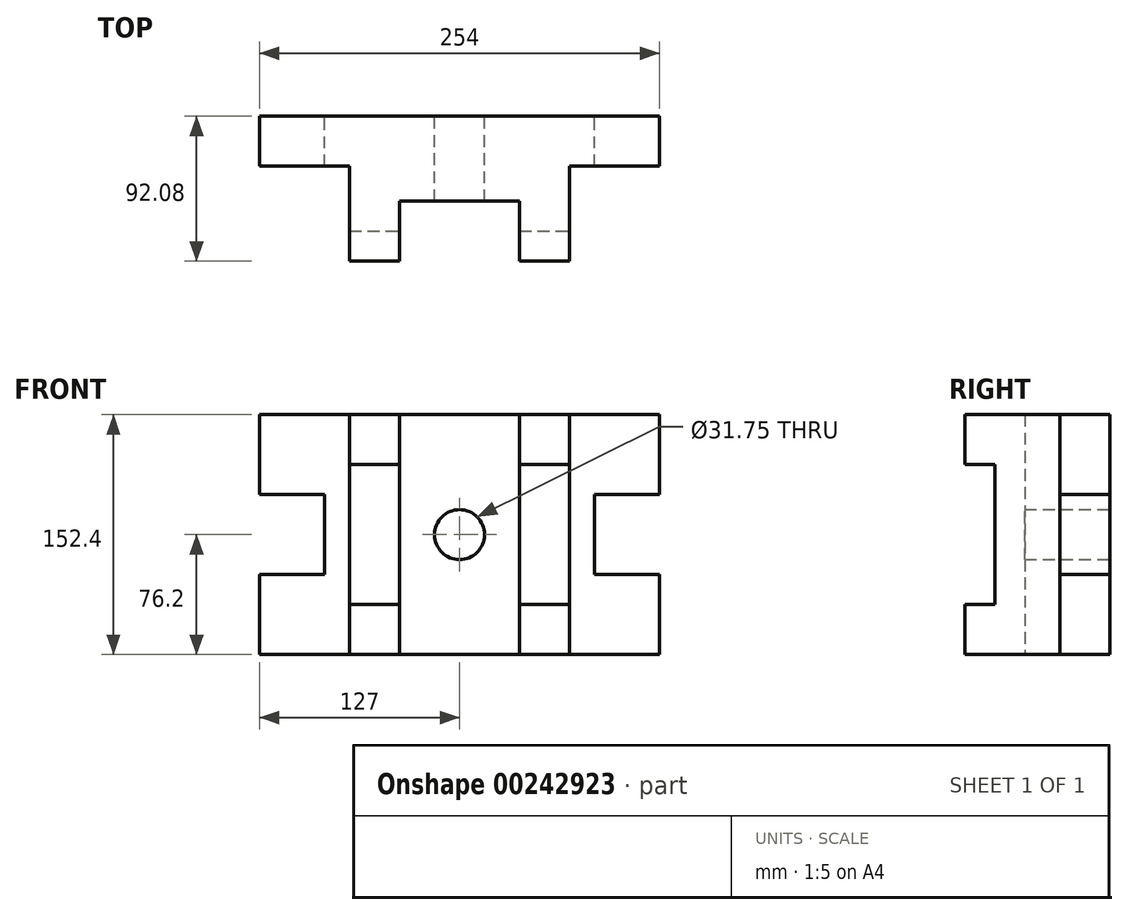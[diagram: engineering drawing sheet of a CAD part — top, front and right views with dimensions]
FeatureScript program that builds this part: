
annotation { "Feature Type Name" : "Feature", "Feature Type Description" : "" }
export const myFeature = defineFeature(function(context is Context, id is Id, definition is map)
    precondition{}
    {
        {
            var Q0;
            Q0=qCreatedBy(makeId("Front.planeOp"),FACE);
            var sketch = newSketch(context, id + "F0", { "sketchPlane" : qUnion([Q0])});
            skLineSegment(sketch, "E0.bottom", {"start": v(127, -76.2) * mm, "end": v(-127, -76.2) * mm});
            skLineSegment(sketch, "E0.top", {"start": v(127, 76.2) * mm, "end": v(-127, 76.2) * mm});
            skLineSegment(sketch, "E0.left", {"start": v(127, -76.2) * mm, "end": v(127, -25.4) * mm});
            skLineSegment(sketch, "E0.right", {"start": v(-127, -76.2) * mm, "end": v(-127, -25.18) * mm});
            skPoint(sketch, "E0.middle", {"position": v(0, 0) * mm});
            skLineSegment(sketch, "E1", {"start": v(-127, -25.18) * mm, "end": v(-127, -25.4) * mm});
            skLineSegment(sketch, "E2", {"start": v(-69.85, 76.2) * mm, "end": v(-69.85, -76.2) * mm});
            skLineSegment(sketch, "E3", {"start": v(-38.1, 76.2) * mm, "end": v(-38.1, -76.2) * mm});
            skLineSegment(sketch, "E4", {"start": v(38.1, 76.2) * mm, "end": v(38.1, -76.2) * mm});
            skLineSegment(sketch, "E5", {"start": v(69.85, -76.2) * mm, "end": v(69.85, 76.2) * mm});
            skLineSegment(sketch, "E6.bottom", {"start": v(-127, 25.4) * mm, "end": v(-85.73, 25.4) * mm});
            skLineSegment(sketch, "E6.top", {"start": v(-127, -25.18) * mm, "end": v(-85.73, -25.18) * mm});
            skLineSegment(sketch, "E6.right", {"start": v(-85.73, 25.4) * mm, "end": v(-85.73, -25.18) * mm});
            skLineSegment(sketch, "E7.bottom", {"start": v(127, 25.4) * mm, "end": v(85.72, 25.4) * mm});
            skLineSegment(sketch, "E7.top", {"start": v(127, -25.4) * mm, "end": v(85.72, -25.4) * mm});
            skLineSegment(sketch, "E7.right", {"start": v(85.72, 25.4) * mm, "end": v(85.72, -25.4) * mm});
            skLineSegment(sketch, "E8", {"start": v(127, -25.4) * mm, "end": v(127, -76.2) * mm});
            skLineSegment(sketch, "E9", {"start": v(-69.85, 44.45) * mm, "end": v(-38.1, 44.45) * mm});
            skLineSegment(sketch, "E10", {"start": v(-69.85, -44.45) * mm, "end": v(-38.1, -44.45) * mm});
            skLineSegment(sketch, "E11", {"start": v(38.1, -44.45) * mm, "end": v(69.85, -44.45) * mm});
            skCircle(sketch, "E12", {"center": v(0, 0) * mm, "radius": 15.88 * mm});
            skLineSegment(sketch, "E13", {"start": v(38.1, 44.45) * mm, "end": v(69.85, 44.45) * mm});
            skLineSegment(sketch, "E14.trimOffspring", {"start": v(127, 25.4) * mm, "end": v(127, 76.2) * mm});
            skLineSegment(sketch, "E15.trimOffspring", {"start": v(-127, 25.4) * mm, "end": v(-127, 76.2) * mm});
            skSolve(sketch);
        }
        {
            var Q0;
            {var subQ7=sQuery(id+"F0.wireOp",EDGE,"E0.right");Q0=makeQuery(id+"F0.imprint","IMPRINT",FACE,{"disambiguationData":[TD([[makeQuery(id+"F0.imprint","IMPRINT",EDGE,{"derivedFrom":subQ7}),-1.0]])]});}
            var Q1;
            Q1=makeQuery(id+"F0.imprint","IMPRINT",FACE,{"disambiguationData":[TD([[makeQuery(id+"F0.imprint","IMPRINT",EDGE,{"derivedFrom":sQuery(id+"F0.wireOp",EDGE,"E7.bottom")}),-1.0]])]});
            extrude(context, id + "F1", {"entities" : qUnion([Q0, Q1]), "depth" : 31.75 * mm});
        }
        {
            var Q0;
            {var subQ5=sQuery(id+"F0.wireOp",EDGE,"E9");Q0=makeQuery(id+"F0.imprint","IMPRINT",FACE,{"disambiguationData":[TD([[makeQuery(id+"F0.imprint","IMPRINT",EDGE,{"derivedFrom":subQ5}),1.0]])]});}
            var Q1;
            {var subQ5=sQuery(id+"F0.wireOp",EDGE,"E10");Q1=makeQuery(id+"F0.imprint","IMPRINT",FACE,{"disambiguationData":[TD([[makeQuery(id+"F0.imprint","IMPRINT",EDGE,{"derivedFrom":subQ5}),-1.0]])]});}
            var Q2;
            {var subQ5=sQuery(id+"F0.wireOp",EDGE,"E11");Q2=makeQuery(id+"F0.imprint","IMPRINT",FACE,{"disambiguationData":[TD([[makeQuery(id+"F0.imprint","IMPRINT",EDGE,{"derivedFrom":subQ5}),-1.0]])]});}
            var Q3;
            {var subQ5=sQuery(id+"F0.wireOp",EDGE,"E13");Q3=makeQuery(id+"F0.imprint","IMPRINT",FACE,{"disambiguationData":[TD([[makeQuery(id+"F0.imprint","IMPRINT",EDGE,{"derivedFrom":subQ5}),1.0]])]});}
            extrude(context, id + "F2", {"entities" : qUnion([Q0, Q1, Q2, Q3]), "depth" : 92.07 * mm});
        }
        {
            var Q0;
            {var subQ0=sQuery(id+"F0.wireOp",EDGE,"E9");Q0=makeQuery(id+"F0.imprint","IMPRINT",FACE,{"disambiguationData":[TD([[makeQuery(id+"F0.imprint","IMPRINT",EDGE,{"derivedFrom":subQ0}),-1.0]])]});}
            var Q1;
            {var subQ0=sQuery(id+"F0.wireOp",EDGE,"E11");Q1=makeQuery(id+"F0.imprint","IMPRINT",FACE,{"disambiguationData":[TD([[makeQuery(id+"F0.imprint","IMPRINT",EDGE,{"derivedFrom":subQ0}),1.0]])]});}
            extrude(context, id + "F3", {"entities" : qUnion([Q0, Q1]), "operationType" : NewBodyOperationType.ADD, "depth" : 73.02 * mm});
        }
        {
            var Q0;
            {var subQ0=sQuery(id+"F0.wireOp",EDGE,"E3");var subQ8=sQuery(id+"F0.wireOp",EDGE,"E0.bottom");var subQ9=makeQuery(id+"F0.imprint","INTERSECT",VERTEX,{"derivedFrom":[subQ8,subQ0]});Q0=makeQuery(id+"F0.imprint","IMPRINT",FACE,{"disambiguationData":[TD([[makeQuery(id+"F0.imprint","IMPRINT",EDGE,{"disambiguationData":[TD([[subQ9,1.0]])],"derivedFrom":subQ8}),-1.0]])]});}
            extrude(context, id + "F4", {"entities" : qUnion([Q0]), "operationType" : NewBodyOperationType.ADD, "depth" : 53.97 * mm});
        }
    });
